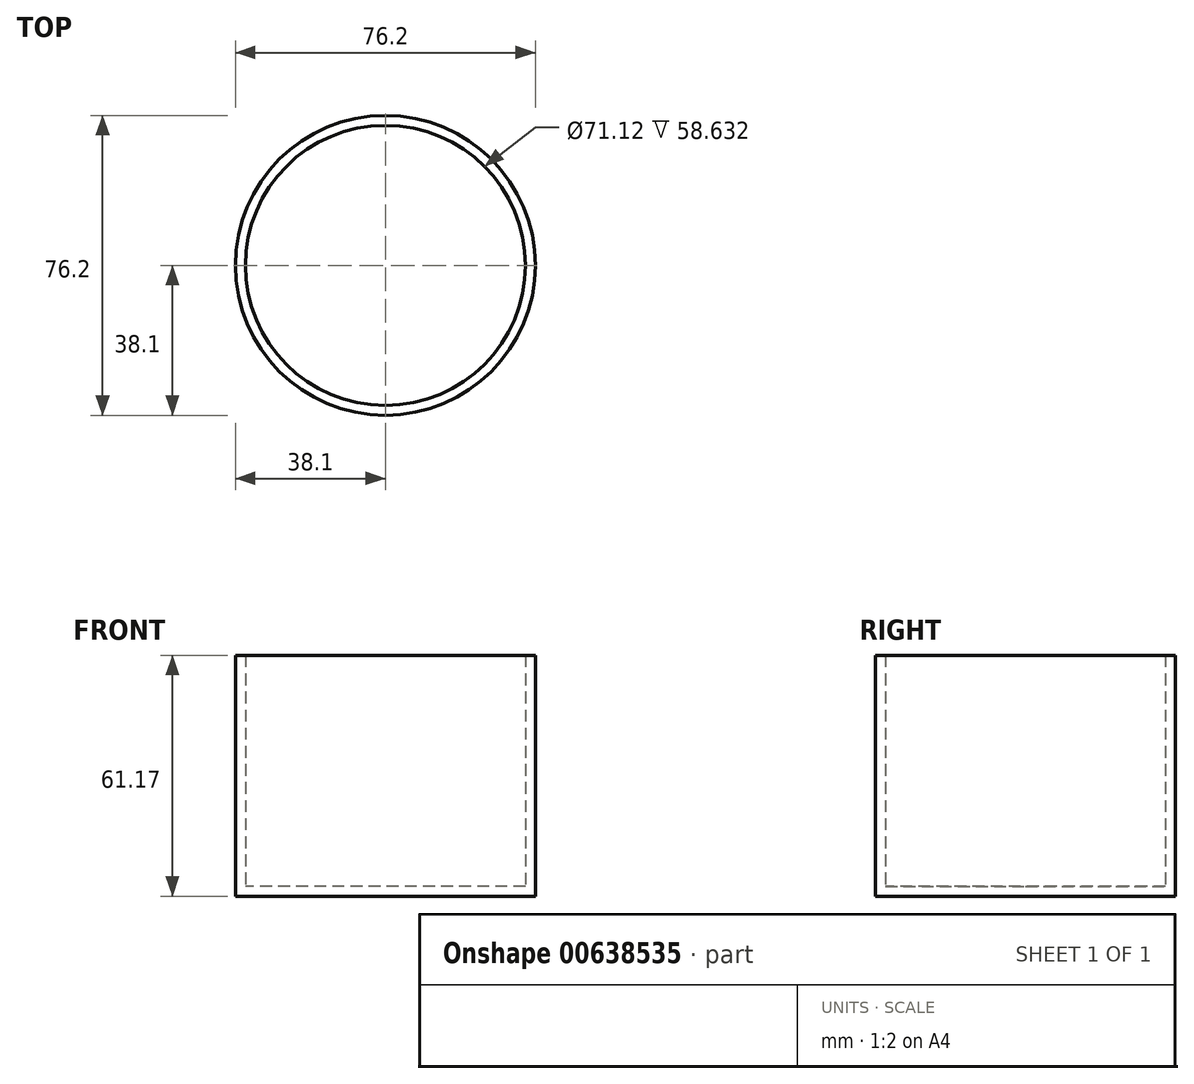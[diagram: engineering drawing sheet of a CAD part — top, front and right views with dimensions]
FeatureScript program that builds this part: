
annotation { "Feature Type Name" : "Feature", "Feature Type Description" : "" }
export const myFeature = defineFeature(function(context is Context, id is Id, definition is map)
    precondition{}
    {
        {
            var Q0;
            Q0=qCreatedBy(makeId("Top.planeOp"),FACE);
            var sketch = newSketch(context, id + "F0", { "sketchPlane" : qUnion([Q0])});
            skLineSegment(sketch, "E0.bottom", {"start": v(38.1, -38.1) * mm, "end": v(-38.1, -38.1) * mm});
            skLineSegment(sketch, "E0.top", {"start": v(38.1, 38.1) * mm, "end": v(-38.1, 38.1) * mm});
            skLineSegment(sketch, "E0.left", {"start": v(38.1, -38.1) * mm, "end": v(38.1, 38.1) * mm});
            skLineSegment(sketch, "E0.right", {"start": v(-38.1, -38.1) * mm, "end": v(-38.1, 38.1) * mm});
            skPoint(sketch, "E0.middle", {"position": v(0, 0) * mm});
            skCircle(sketch, "E1", {"center": v(0, 0) * mm, "radius": 38.1 * mm});
            skSolve(sketch);
        }
        {
            var Q0;
            {var subQ0=sQuery(id+"F0.wireOp",EDGE,"E1");var subQ1=makeQuery(id+"F0.imprint","INTERSECT",VERTEX,{"derivedFrom":[sQuery(id+"F0.wireOp",EDGE,"E0.top"),subQ0]});Q0=makeQuery(id+"F0.imprint","IMPRINT",FACE,{"disambiguationData":[TD([[makeQuery(id+"F0.imprint","IMPRINT",EDGE,{"disambiguationData":[TD([[subQ1,1.0]])],"derivedFrom":subQ0}),1.0]])]});}
            extrude(context, id + "F1", {"entities" : qUnion([Q0]), "depth" : 61.17 * mm, "offsetDistance" : 25.4 * mm});
        }
        {
            var Q0;
            Q0=makeQuery(id+"F1.opExtrude","CAP_FACE",FACE,{"disambiguationData":[OSD([sQuery(id+"F0.wireOp",EDGE,"E1")])],"isStart":false});
            shell(context, id + "F2", {"entities" : qUnion([Q0]), "thickness" : 2.54 * mm});
        }
    });
